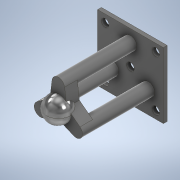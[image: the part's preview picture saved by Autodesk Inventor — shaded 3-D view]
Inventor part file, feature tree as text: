
AUTODESK INVENTOR PART (.ipt)
format: ipt  version: 2022 (Build 260153000, 153)  size: 225,792 bytes
history: native  units: mm
features: other x3, extrude x3, sketch x3, hole x1, pattern_circular x1
ambient origin geometry x8: Origin, YZ Plane, XZ Plane, XY Plane, X Axis, Y Axis, Z Axis, Center Point
bodies: Body1 (feature_tree)
feature tree (11):
  other  "フォーム1"
  other  "作業平面1"
  extrude  "押し出し1"  [1 undecoded]
  hole  "穴1"  [1 undecoded]
  sketch  "スケッチ3"
  extrude  "押し出し2"  Depth=26.0mm
  extrude  "押し出し3"  Depth=1.5mm TaperAngle=0.0deg
  pattern_circular  "円形状パターン2"  [2 undecoded]
  sketch  "スケッチ2"
  sketch  "スケッチ4"
  other  "ソリッド1"
note: 4 required parameter values undecoded (feature->parameter linkage not recoverable at this tier; creation-order binding heuristic only, values carry confidence <= 0.55)
